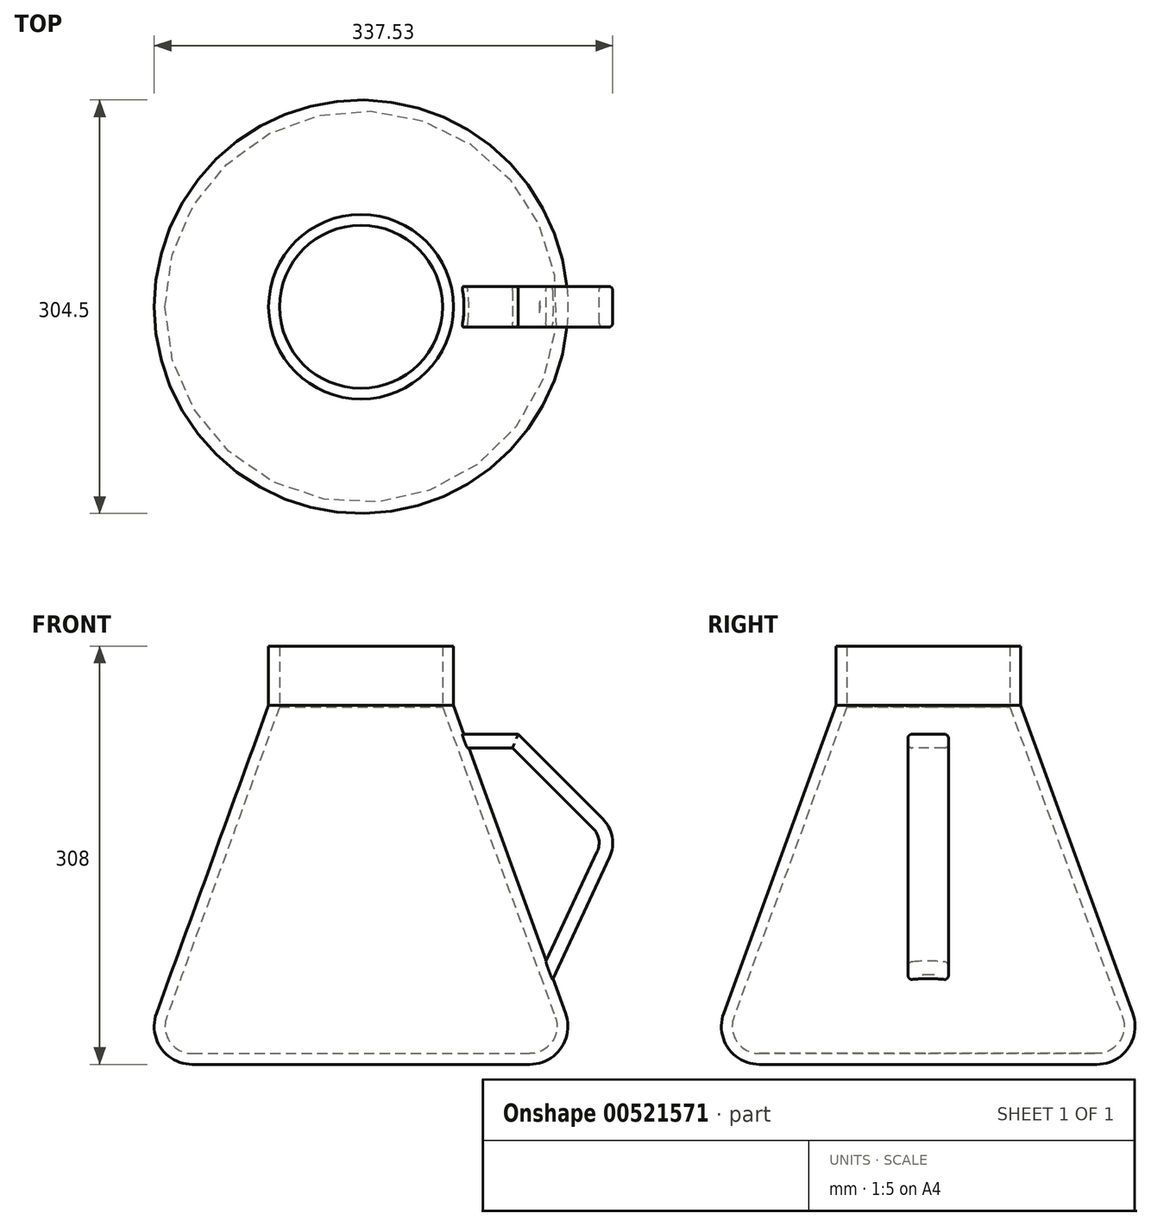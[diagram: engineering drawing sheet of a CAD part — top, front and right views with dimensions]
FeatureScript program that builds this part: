
annotation { "Feature Type Name" : "Feature", "Feature Type Description" : "" }
export const myFeature = defineFeature(function(context is Context, id is Id, definition is map)
    precondition{}
    {
        {
            var Q0;
            Q0=qCreatedBy(makeId("Right.planeOp"),FACE);
            var sketch = newSketch(context, id + "F0", { "sketchPlane" : qUnion([Q0])});
            skLineSegment(sketch, "E0", {"start": v(-60, 255) * mm, "end": v(-143.04, 26.84) * mm});
            skLineSegment(sketch, "E1", {"start": v(-124.25, 0) * mm, "end": v(0, 0) * mm});
            skLineSegment(sketch, "E2", {"start": v(0, 0) * mm, "end": v(0, 300) * mm});
            skLineSegment(sketch, "E3", {"start": v(-60, 255) * mm, "end": v(-60, 300) * mm});
            skPoint(sketch, "E4.visualSharp", {"position": v(-152.81, 0) * mm});
            skArc(sketch, "E4.filletArc", {"start": v(-143.04, 26.84) * mm, "mid": v(-140.63, 8.53) * mm, "end": v(-124.25, 0) * mm});
            skLineSegment(sketch, "E5.0", {"start": v(-68, 256.41) * mm, "end": v(-68, 300) * mm});
            skLineSegment(sketch, "E5.1", {"start": v(-68, 256.41) * mm, "end": v(-150.56, 29.58) * mm});
            skArc(sketch, "E5.2", {"start": v(-150.56, 29.58) * mm, "mid": v(-147.19, 3.94) * mm, "end": v(-124.25, -8) * mm});
            skLineSegment(sketch, "E5.3", {"start": v(-124.25, -8) * mm, "end": v(0, -8) * mm});
            skLineSegment(sketch, "E6", {"start": v(-68, 300) * mm, "end": v(-60, 300) * mm});
            skLineSegment(sketch, "E7", {"start": v(0, 0) * mm, "end": v(0, -8) * mm});
            skSolve(sketch);
        }
        {
            var Q0;
            Q0=makeQuery(id+"F0.imprint","IMPRINT",FACE,{"disambiguationData":[TD([[makeQuery(id+"F0.imprint","IMPRINT",EDGE,{"derivedFrom":sQuery(id+"F0.wireOp",EDGE,"E0")}),-1.0]])]});
            var Q1;
            Q1=sQuery(id+"F0.wireOp",EDGE,"E2");
            revolve(context, id + "F1", {"entities" : qUnion([Q0]), "axis" : qUnion([Q1]), "revolveType" : RevolveType.FULL});
        }
        {
            var Q0;
            Q0=qCreatedBy(makeId("Right.planeOp"),FACE);
            var sketch = newSketch(context, id + "F2", { "sketchPlane" : qUnion([Q0])});
            skPoint(sketch, "E8.middle", {"position": v(0, 0) * mm});
            skLineSegment(sketch, "E9.bottom", {"start": v(12, 225) * mm, "end": v(-12, 225) * mm});
            skLineSegment(sketch, "E9.top", {"start": v(12, 235) * mm, "end": v(-12, 235) * mm});
            skLineSegment(sketch, "E9.left", {"start": v(15, 228) * mm, "end": v(15, 232) * mm});
            skLineSegment(sketch, "E9.right", {"start": v(-15, 228) * mm, "end": v(-15, 232) * mm});
            skPoint(sketch, "E9.middle", {"position": v(0, 230) * mm});
            skPoint(sketch, "E10.visualSharp", {"position": v(-15, 235) * mm});
            skArc(sketch, "E10.filletArc", {"start": v(-12, 235) * mm, "mid": v(-14.12, 234.12) * mm, "end": v(-15, 232) * mm});
            skPoint(sketch, "E11.visualSharp", {"position": v(15, 235) * mm});
            skArc(sketch, "E11.filletArc", {"start": v(15, 232) * mm, "mid": v(14.12, 234.12) * mm, "end": v(12, 235) * mm});
            skPoint(sketch, "E12.visualSharp", {"position": v(15, 225) * mm});
            skArc(sketch, "E12.filletArc", {"start": v(12, 225) * mm, "mid": v(14.12, 225.88) * mm, "end": v(15, 228) * mm});
            skPoint(sketch, "E13.visualSharp", {"position": v(-15, 225) * mm});
            skArc(sketch, "E13.filletArc", {"start": v(-15, 228) * mm, "mid": v(-14.12, 225.88) * mm, "end": v(-12, 225) * mm});
            skSolve(sketch);
        }
        {
            var Q0;
            Q0=qCreatedBy(makeId("Front.planeOp"),FACE);
            var sketch = newSketch(context, id + "F3", { "sketchPlane" : qUnion([Q0])});
            skLineSegment(sketch, "E14", {"start": v(0, 230) * mm, "end": v(113.61, 230) * mm});
            skLineSegment(sketch, "E15", {"start": v(68, 256.41) * mm, "end": v(150.56, 29.58) * mm, "construction": true});
            skPoint(sketch, "E16", {"position": v(77.61, 230) * mm});
            skLineSegment(sketch, "E17", {"start": v(113.61, 230) * mm, "end": v(174.42, 169.2) * mm});
            skLineSegment(sketch, "E18", {"start": v(178.4, 146.6) * mm, "end": v(136.13, 55.95) * mm});
            skPoint(sketch, "E19.visualSharp", {"position": v(184.32, 159.29) * mm});
            skArc(sketch, "E19.filletArc", {"start": v(178.4, 146.6) * mm, "mid": v(180.22, 153.52) * mm, "end": v(179.48, 160.64) * mm});
            skArc(sketch, "E20.filletArc", {"start": v(178.4, 146.6) * mm, "mid": v(179.97, 158.52) * mm, "end": v(174.42, 169.2) * mm});
            skSolve(sketch);
        }
        {
            var Q0;
            Q0 = qSketchRegion(id + "F2", true);
            var Q1;
            Q1=sQuery(id+"F3.wireOp",EDGE,"E14");
            var Q2;
            Q2=sQuery(id+"F3.wireOp",EDGE,"E17");
            var Q3;
            Q3=sQuery(id+"F3.wireOp",EDGE,"E20.filletArc");
            var Q4;
            Q4=sQuery(id+"F3.wireOp",EDGE,"E18");
            sweep(context, id + "F4", {"operationType" : NewBodyOperationType.ADD, "profiles" : qUnion([Q0]), "path" : qUnion([Q1, Q2, Q3, Q4])});
        }
        {
            var Q0;
            Q0=makeQuery(id+"F4.opSweep","CAP_FACE",FACE,{"disambiguationData":[OSD([sQuery(id+"F2.wireOp",EDGE,"E9.bottom"),sQuery(id+"F2.wireOp",EDGE,"E9.top"),sQuery(id+"F2.wireOp",EDGE,"E9.left"),sQuery(id+"F2.wireOp",EDGE,"E9.right"),sQuery(id+"F2.wireOp",EDGE,"E10.filletArc"),sQuery(id+"F2.wireOp",EDGE,"E11.filletArc"),sQuery(id+"F2.wireOp",EDGE,"E12.filletArc"),sQuery(id+"F2.wireOp",EDGE,"E13.filletArc"),sQuery(id+"F3.wireOp",VERTEX,"E14.start")])],"isStart":true});
            var sketch = newSketch(context, id + "F5", { "sketchPlane" : qUnion([Q0])});
            skLineSegment(sketch, "E21.0", {"start": v(-12, 235) * mm, "end": v(12, 235) * mm});
            skPoint(sketch, "E22.0", {"position": v(-14.12, 234.12) * mm});
            skArc(sketch, "E23.0", {"start": v(-15, 232) * mm, "mid": v(-14.12, 234.12) * mm, "end": v(-12, 235) * mm});
            skLineSegment(sketch, "E24.0", {"start": v(-15, 228) * mm, "end": v(-15, 232) * mm});
            skArc(sketch, "E25.0", {"start": v(-12, 225) * mm, "mid": v(-14.12, 225.88) * mm, "end": v(-15, 228) * mm});
            skLineSegment(sketch, "E26.0", {"start": v(12, 225) * mm, "end": v(-12, 225) * mm});
            skArc(sketch, "E27.0", {"start": v(15, 228) * mm, "mid": v(14.12, 225.88) * mm, "end": v(12, 225) * mm});
            skPoint(sketch, "E28.0", {"position": v(15, 230) * mm});
            skLineSegment(sketch, "E29.0", {"start": v(15, 232) * mm, "end": v(15, 228) * mm});
            skArc(sketch, "E30.0", {"start": v(12, 235) * mm, "mid": v(14.12, 234.12) * mm, "end": v(15, 232) * mm});
            skSolve(sketch);
        }
        {
            var Q0;
            Q0 = qSketchRegion(id + "F5", true);
            var Q1;
            Q1=makeQuery(id+"F1.opRevolve","SWEPT_FACE",FACE,{"disambiguationData":[OSD([sQuery(id+"F0.wireOp",EDGE,"E0")])]});
            extrude(context, id + "F6", {"entities" : qUnion([Q0]), "operationType" : NewBodyOperationType.REMOVE, "endBound" : BoundingType.UP_TO_SURFACE, "oppositeDirection" : true, "depth" : 25 * mm, "endBoundEntityFace" : qUnion([Q1]), "offsetDistance" : 25 * mm});
        }
    });
